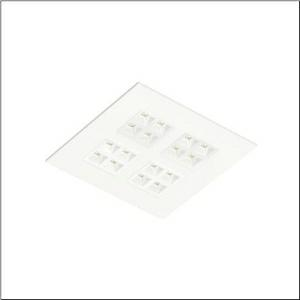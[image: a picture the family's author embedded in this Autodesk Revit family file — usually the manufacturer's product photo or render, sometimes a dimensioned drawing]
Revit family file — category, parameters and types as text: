
# Revit family: silica_r__31_square_51my6nds34wa_8f6b
name_source: partatom
category: Lighting Fixtures
units: mm (PartAtom-declared; Revit-internal decimal feet)

## family parameters
Cut with Voids When Loaded = No
Host = Face
Light Source = No
Part Type = Normal
Room Calculation Point = No
Round Connector Dimension = Use Diameter
Shared = No

## types (1)
- --- (1 x LED, 6230 lm, 38.5 W, 3000K)
    Apparent Load = 39 VA
    CIE Flux Codes = 81 99 100 100 100
    Color Rendering = 80
    Color Temperature = 3000K
    Default Elevation = 1800 mm
    Description = Silica® 31 Square, office luminaire, primary light control with lens, of PMMA, primary anti-glare with reflector, of PC, white, light emission: direct distribution, primary light characteristic: symmetric, installation type: lay-in mounting, LED, rated luminous flux: 4.540lm, luminous efficacy: 162lm/W, light colour: 830, colour temperature: 3000K, control gear: DALI 2, Multilumen, with terminal, 5-pole, mains connection: 220..240V, AC, 50/60Hz, rated input power: 28W, luminaire housing, of sheet steel, coated, traffic white (RAL 9016), module: M600, length: 595mm, width: 595mm, height: 43mm, protection rating (complete): IP20, insulation class (complete): insulation class II (safety insulation), certification: CE, impact resistance: IK03, permissible operating ambient temperature: -20..+35°C, standard: EN 50419, packaging unit: 1 piece
    Height = 0 mm  [stored 0 ft]
    Lamp = 1 x LED
    Lamp Light Flux = 6230 lm
    Lamp Power = 38.5 W
    Lamp count = 1
    Length = 595 mm
    Luminous efficacy = 162 lm/W
    Manufacturer = Siteco
    ModVariant = No
    Model = 51MY6NDS34WA
    Mounting Place = Ceiling
    Mounting Type = Recessed
    Number of Poles = 1
    OnlyDefault = Yes
    Power Factor = 1
    Product Name = Silica® 31 Square
    Product group = office luminaire | ceiling recessed
    ProductGroupID = 401
    Protection Class = Protection class II
    Protection Degree = IP 20
    RLX_Detail_Level = 1
    RLX_Emergency_Light_Flux = 0 lm
    RLX_Emergency_Type = 0
    RLX_Emergency_Type_DB = No
    RlxData = <blob elided: 27985 chars, md5=c423b743>
    Socket = socket
    Standby Power = 0 W
    System Light Flux = 6230 lm
    System Power = 39 W
    Type Comments = factory setting: luminous flux: 100 % | (OFF | OFF | OFF | OFF) | 1050 mA
    Type Image = l_1313651.jpg
    URL = http://relux.com
    VarID = @adj_035954
    Voltage = 0 V
    Weight = 0.00 kg
    Width = 595 mm

note: [stored X ft] marks values corroborated as IEEE doubles in the binary element streams (Revit-internal decimal feet)

## geometry (parser evidence)
native form markers: Blend x4, Sweep x12
no freeform markers — native parametric forms only
